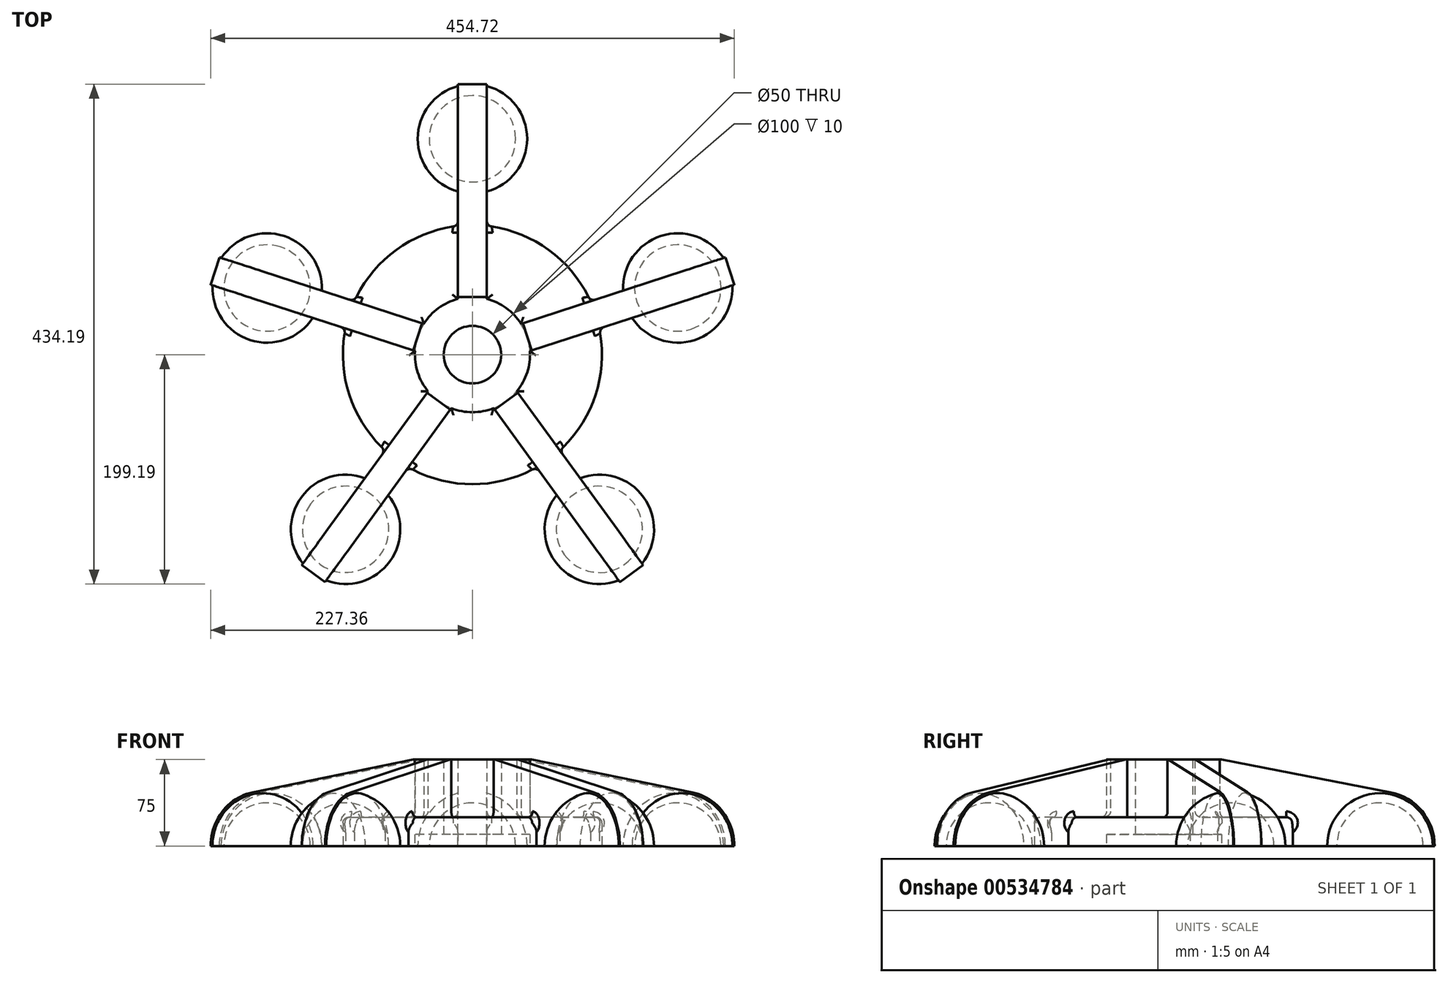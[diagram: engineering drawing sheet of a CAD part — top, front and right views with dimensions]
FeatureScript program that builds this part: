
annotation { "Feature Type Name" : "Feature", "Feature Type Description" : "" }
export const myFeature = defineFeature(function(context is Context, id is Id, definition is map)
    precondition{}
    {
        {
            var Q0;
            Q0=qCreatedBy(makeId("Right.planeOp"),FACE);
            var sketch = newSketch(context, id + "F0", { "sketchPlane" : qUnion([Q0])});
            skCircle(sketch, "E0", {"center": v(187.5, 0) * mm, "radius": 37.5 * mm});
            skCircle(sketch, "E1", {"center": v(187.5, 0) * mm, "radius": 47.5 * mm});
            skLineSegment(sketch, "E2", {"start": v(140, 0) * mm, "end": v(235, 0) * mm});
            skLineSegment(sketch, "E3", {"start": v(187.5, 47.5) * mm, "end": v(187.5, -47.5) * mm});
            skLineSegment(sketch, "E4", {"start": v(0, 0) * mm, "end": v(140, 0) * mm});
            skLineSegment(sketch, "E5", {"start": v(0, 0) * mm, "end": v(0, 75) * mm});
            skLineSegment(sketch, "E6", {"start": v(0, 75) * mm, "end": v(50, 75) * mm});
            skLineSegment(sketch, "E7", {"start": v(50, 75) * mm, "end": v(196.53, 46.63) * mm});
            skSolve(sketch);
        }
        {
            var Q0;
            {var subQ0=sQuery(id+"F0.wireOp",EDGE,"E3");var subQ1=sQuery(id+"F0.wireOp",EDGE,"E0");var subQ2=makeQuery(id+"F0.imprint","INTERSECT",VERTEX,{"disambiguationData":[OD(0.0)],"derivedFrom":[subQ1,subQ0]});Q0=makeQuery(id+"F0.imprint","IMPRINT",FACE,{"disambiguationData":[TD([[makeQuery(id+"F0.imprint","IMPRINT",EDGE,{"disambiguationData":[TD([[subQ2,1.0]])],"derivedFrom":subQ1}),-1.0]])]});}
            var Q1;
            Q1=sQuery(id+"F0.wireOp",EDGE,"E3");
            revolve(context, id + "F1", {"entities" : qUnion([Q0]), "axis" : qUnion([Q1]), "revolveType" : RevolveType.FULL});
        }
        {
            var Q0;
            Q0=qCreatedBy(makeId("Right.planeOp"),FACE);
            var sketch = newSketch(context, id + "F2", { "sketchPlane" : qUnion([Q0])});
            skCircle(sketch, "E8", {"center": v(187.5, 0) * mm, "radius": 37.5 * mm});
            skCircle(sketch, "E9", {"center": v(187.5, 0) * mm, "radius": 47.5 * mm});
            skLineSegment(sketch, "E10", {"start": v(140, 0) * mm, "end": v(235, 0) * mm});
            skLineSegment(sketch, "E11", {"start": v(187.5, 47.5) * mm, "end": v(187.5, -47.5) * mm});
            skLineSegment(sketch, "E12", {"start": v(0, 0) * mm, "end": v(140, 0) * mm});
            skLineSegment(sketch, "E13", {"start": v(0, 0) * mm, "end": v(0, 75) * mm});
            skLineSegment(sketch, "E14", {"start": v(0, 75) * mm, "end": v(50, 75) * mm});
            skLineSegment(sketch, "E15", {"start": v(50, 75) * mm, "end": v(196.53, 46.63) * mm});
            skSolve(sketch);
        }
        {
            var Q0;
            {var subQ0=sQuery(id+"F2.wireOp",EDGE,"E12");Q0=makeQuery(id+"F2.imprint","IMPRINT",FACE,{"disambiguationData":[TD([[makeQuery(id+"F2.imprint","IMPRINT",EDGE,{"derivedFrom":subQ0}),1.0]])]});}
            var Q1;
            {var subQ3=sQuery(id+"F2.wireOp",EDGE,"E8");var subQ6=sQuery(id+"F2.wireOp",EDGE,"E11");var subQ8=makeQuery(id+"F2.imprint","INTERSECT",VERTEX,{"disambiguationData":[OD(0.0)],"derivedFrom":[subQ3,subQ6]});Q1=makeQuery(id+"F2.imprint","IMPRINT",FACE,{"disambiguationData":[TD([[makeQuery(id+"F2.imprint","IMPRINT",EDGE,{"disambiguationData":[TD([[subQ8,1.0]])],"derivedFrom":subQ3}),-1.0]])]});}
            var Q2;
            {var subQ0=sQuery(id+"F2.wireOp",EDGE,"E11");var subQ1=sQuery(id+"F2.wireOp",EDGE,"E8");var subQ2=makeQuery(id+"F2.imprint","INTERSECT",VERTEX,{"disambiguationData":[OD(0.0)],"derivedFrom":[subQ1,subQ0]});Q2=makeQuery(id+"F2.imprint","IMPRINT",FACE,{"disambiguationData":[TD([[makeQuery(id+"F2.imprint","IMPRINT",EDGE,{"disambiguationData":[TD([[subQ2,-1.0]])],"derivedFrom":subQ1}),-1.0]])]});}
            extrude(context, id + "F3", {"entities" : qUnion([Q0, Q1, Q2]), "operationType" : NewBodyOperationType.ADD, "endBound" : BoundingType.SYMMETRIC, "depth" : 25 * mm, "offsetDistance" : 25 * mm});
        }
        {
            var Q0;
            Q0=qCreatedBy(makeId("Top.planeOp"),FACE);
            var sketch = newSketch(context, id + "F4", { "sketchPlane" : qUnion([Q0])});
            skCircle(sketch, "E16", {"center": v(0, 0) * mm, "radius": 25 * mm});
            skCircle(sketch, "E17", {"center": v(0, 0) * mm, "radius": 50 * mm});
            skSolve(sketch);
        }
        {
            var Q0;
            Q0=makeQuery(id+"F4.imprint","IMPRINT",FACE,{"disambiguationData":[TD([[makeQuery(id+"F4.imprint","IMPRINT",EDGE,{"derivedFrom":sQuery(id+"F4.wireOp",EDGE,"E16")}),1.0]])]});
            extrude(context, id + "F5", {"entities" : qUnion([Q0]), "operationType" : NewBodyOperationType.REMOVE, "endBound" : BoundingType.THROUGH_ALL, "depth" : 25 * mm, "offsetDistance" : 25 * mm});
        }
        {
            var Q0;
            Q0=qCreatedBy(makeId("Top.planeOp"),FACE);
            var sketch = newSketch(context, id + "F6", { "sketchPlane" : qUnion([Q0])});
            skCircle(sketch, "E18", {"center": v(0, 0) * mm, "radius": 50 * mm});
            skCircle(sketch, "E19", {"center": v(0, 0) * mm, "radius": 25 * mm});
            skSolve(sketch);
        }
        {
            var Q0;
            Q0 = qSketchRegion(id + "F6", true);
            var Q1;
            Q1=makeQuery(id+"F3.opExtrude","SWEPT_FACE",FACE,{"disambiguationData":[OSD([sQuery(id+"F2.wireOp",EDGE,"E14")])]});
            extrude(context, id + "F7", {"entities" : qUnion([Q0]), "operationType" : NewBodyOperationType.ADD, "endBound" : BoundingType.UP_TO_SURFACE, "depth" : 25 * mm, "endBoundEntityFace" : qUnion([Q1]), "offsetDistance" : 25 * mm});
        }
        {
            var Q0;
            Q0=makeQuery(id+"F1.opRevolve","SWEPT_BODY",BODY,{"disambiguationData":[OSD([sQuery(id+"F0.wireOp",EDGE,"E0"),sQuery(id+"F0.wireOp",EDGE,"E1"),sQuery(id+"F0.wireOp",EDGE,"E2"),sQuery(id+"F0.wireOp",EDGE,"E3")])]});
            var Q1;
            Q1=makeQuery(id+"F5.boolean.opBoolean","COPY",FACE,{"derivedFrom":makeQuery(id+"F5.opExtrude","SWEPT_FACE",FACE,{"disambiguationData":[OSD([sQuery(id+"F4.wireOp",EDGE,"E16")])]})});
            circularPattern(context, id + "F8", {"operationType" : NewBodyOperationType.ADD, "entities" : qUnion([Q0]), "axis" : qUnion([Q1]), "angle" : 360 * degree, "instanceCount" : 5, "equalSpace" : true});
        }
        {
            var Q0;
            Q0=qCreatedBy(makeId("Top.planeOp"),FACE);
            var sketch = newSketch(context, id + "F9", { "sketchPlane" : qUnion([Q0])});
            skCircle(sketch, "E20", {"center": v(0, 0) * mm, "radius": 112.5 * mm});
            skCircle(sketch, "E21", {"center": v(0, 0) * mm, "radius": 25 * mm});
            skSolve(sketch);
        }
        {
            var Q0;
            Q0=makeQuery(id+"F9.imprint","IMPRINT",FACE,{"disambiguationData":[TD([[makeQuery(id+"F9.imprint","IMPRINT",EDGE,{"derivedFrom":sQuery(id+"F9.wireOp",EDGE,"E20")}),1.0]])]});
            extrude(context, id + "F10", {"entities" : qUnion([Q0]), "operationType" : NewBodyOperationType.ADD, "depth" : 25 * mm, "offsetDistance" : 25 * mm});
        }
        {
            var Q0;
            {var subQ0=sQuery(id+"F2.wireOp",EDGE,"E15");var subQ1=sQuery(id+"F2.wireOp",EDGE,"E14");var subQ2=sQuery(id+"F2.wireOp",EDGE,"E13");var subQ3=sQuery(id+"F2.wireOp",EDGE,"E12");var subQ4=sQuery(id+"F2.wireOp",EDGE,"E10");var subQ5=sQuery(id+"F2.wireOp",EDGE,"E9");var subQ6=sQuery(id+"F2.wireOp",EDGE,"E8");var subQ7=sQuery(id+"F9.wireOp",EDGE,"E20");Q0=makeQuery(id+"F10.boolean.opBoolean","SPLIT",FACE,{"disambiguationData":[TD([makeQuery(id+"F3.opExtrude","CAP_FACE",FACE,{"disambiguationData":[OSD([subQ6,subQ5,subQ4,subQ3,subQ2,subQ1,subQ0])],"isStart":true})])],"derivedFrom":makeQuery(id+"F10.opExtrude","CAP_FACE",FACE,{"disambiguationData":[OSD([subQ7,sQuery(id+"F9.wireOp",EDGE,"MwNo4NWU-MyD3-ABLd-Lk5J-k6dSSuvND8tt")])],"isStart":false})});}
            var Q1;
            {var subQ0=sQuery(id+"F9.wireOp",EDGE,"E20");var subQ1=sQuery(id+"F2.wireOp",EDGE,"E15");var subQ2=sQuery(id+"F2.wireOp",EDGE,"E14");var subQ3=sQuery(id+"F2.wireOp",EDGE,"E13");var subQ4=sQuery(id+"F2.wireOp",EDGE,"E12");var subQ5=sQuery(id+"F2.wireOp",EDGE,"E10");var subQ6=sQuery(id+"F2.wireOp",EDGE,"E9");var subQ7=sQuery(id+"F2.wireOp",EDGE,"E8");Q1=makeQuery(id+"F10.boolean.opBoolean","SPLIT",FACE,{"disambiguationData":[TD([makeQuery(id+"F8.opPattern","COPY",FACE,{"derivedFrom":makeQuery(id+"F3.opExtrude","CAP_FACE",FACE,{"disambiguationData":[OSD([subQ7,subQ6,subQ5,subQ4,subQ3,subQ2,subQ1])],"isStart":true}),"instanceName":"1"})])],"derivedFrom":makeQuery(id+"F10.opExtrude","CAP_FACE",FACE,{"disambiguationData":[OSD([subQ0,sQuery(id+"F9.wireOp",EDGE,"MwNo4NWU-MyD3-ABLd-Lk5J-k6dSSuvND8tt")])],"isStart":false})});}
            var Q2;
            {var subQ0=sQuery(id+"F2.wireOp",EDGE,"E15");var subQ1=sQuery(id+"F2.wireOp",EDGE,"E14");var subQ2=sQuery(id+"F2.wireOp",EDGE,"E13");var subQ3=sQuery(id+"F2.wireOp",EDGE,"E12");var subQ4=sQuery(id+"F2.wireOp",EDGE,"E10");var subQ5=sQuery(id+"F2.wireOp",EDGE,"E9");var subQ6=sQuery(id+"F2.wireOp",EDGE,"E8");var subQ7=sQuery(id+"F9.wireOp",EDGE,"E20");Q2=makeQuery(id+"F10.boolean.opBoolean","SPLIT",FACE,{"disambiguationData":[TD([makeQuery(id+"F8.opPattern","COPY",FACE,{"derivedFrom":makeQuery(id+"F3.opExtrude","CAP_FACE",FACE,{"disambiguationData":[OSD([subQ6,subQ5,subQ4,subQ3,subQ2,subQ1,subQ0])],"isStart":true}),"instanceName":"2"})])],"derivedFrom":makeQuery(id+"F10.opExtrude","CAP_FACE",FACE,{"disambiguationData":[OSD([subQ7,sQuery(id+"F9.wireOp",EDGE,"MwNo4NWU-MyD3-ABLd-Lk5J-k6dSSuvND8tt")])],"isStart":false})});}
            var Q3;
            {var subQ0=sQuery(id+"F9.wireOp",EDGE,"E20");var subQ1=sQuery(id+"F2.wireOp",EDGE,"E15");var subQ2=sQuery(id+"F2.wireOp",EDGE,"E14");var subQ3=sQuery(id+"F2.wireOp",EDGE,"E13");var subQ4=sQuery(id+"F2.wireOp",EDGE,"E12");var subQ5=sQuery(id+"F2.wireOp",EDGE,"E10");var subQ6=sQuery(id+"F2.wireOp",EDGE,"E9");var subQ7=sQuery(id+"F2.wireOp",EDGE,"E8");Q3=makeQuery(id+"F10.boolean.opBoolean","SPLIT",FACE,{"disambiguationData":[TD([makeQuery(id+"F8.opPattern","COPY",FACE,{"derivedFrom":makeQuery(id+"F3.opExtrude","CAP_FACE",FACE,{"disambiguationData":[OSD([subQ7,subQ6,subQ5,subQ4,subQ3,subQ2,subQ1])],"isStart":true}),"instanceName":"3"})])],"derivedFrom":makeQuery(id+"F10.opExtrude","CAP_FACE",FACE,{"disambiguationData":[OSD([subQ0,sQuery(id+"F9.wireOp",EDGE,"MwNo4NWU-MyD3-ABLd-Lk5J-k6dSSuvND8tt")])],"isStart":false})});}
            var Q4;
            {var subQ0=sQuery(id+"F2.wireOp",EDGE,"E15");var subQ1=sQuery(id+"F2.wireOp",EDGE,"E14");var subQ2=sQuery(id+"F2.wireOp",EDGE,"E13");var subQ3=sQuery(id+"F2.wireOp",EDGE,"E12");var subQ4=sQuery(id+"F2.wireOp",EDGE,"E10");var subQ5=sQuery(id+"F2.wireOp",EDGE,"E9");var subQ6=sQuery(id+"F2.wireOp",EDGE,"E8");var subQ7=sQuery(id+"F9.wireOp",EDGE,"E20");Q4=makeQuery(id+"F10.boolean.opBoolean","SPLIT",FACE,{"disambiguationData":[TD([makeQuery(id+"F3.opExtrude","CAP_FACE",FACE,{"disambiguationData":[OSD([subQ6,subQ5,subQ4,subQ3,subQ2,subQ1,subQ0])],"isStart":false})])],"derivedFrom":makeQuery(id+"F10.opExtrude","CAP_FACE",FACE,{"disambiguationData":[OSD([subQ7,sQuery(id+"F9.wireOp",EDGE,"MwNo4NWU-MyD3-ABLd-Lk5J-k6dSSuvND8tt")])],"isStart":false})});}
            var Q5;
            Q5=makeQuery(id+"F10.boolean.opBoolean","INTERSECT",EDGE,{"derivedFrom":[makeQuery(id+"F8.opPattern","COPY",FACE,{"derivedFrom":makeQuery(id+"F3.opExtrude","CAP_FACE",FACE,{"disambiguationData":[OSD([sQuery(id+"F2.wireOp",EDGE,"E8"),sQuery(id+"F2.wireOp",EDGE,"E9"),sQuery(id+"F2.wireOp",EDGE,"E10"),sQuery(id+"F2.wireOp",EDGE,"E12"),sQuery(id+"F2.wireOp",EDGE,"E13"),sQuery(id+"F2.wireOp",EDGE,"E14"),sQuery(id+"F2.wireOp",EDGE,"E15")])],"isStart":false}),"instanceName":"2"}),makeQuery(id+"F10.opExtrude","CAP_FACE",FACE,{"disambiguationData":[OSD([sQuery(id+"F9.wireOp",EDGE,"E20"),sQuery(id+"F9.wireOp",EDGE,"MwNo4NWU-MyD3-ABLd-Lk5J-k6dSSuvND8tt")])],"isStart":false})]});
            fillet(context, id + "F11", {"entities" : qUnion([Q0, Q1, Q2, Q3, Q4, Q5]), "radius" : 5 * mm, "tangentPropagation" : true, "allowEdgeOverflow" : false});
        }
        {
            var Q0;
            Q0=qCreatedBy(makeId("Top.planeOp"),FACE);
            var sketch = newSketch(context, id + "F12", { "sketchPlane" : qUnion([Q0])});
            skCircle(sketch, "E22", {"center": v(0, 0) * mm, "radius": 50 * mm});
            skSolve(sketch);
        }
        {
            var Q0;
            Q0 = qSketchRegion(id + "F12", true);
            extrude(context, id + "F13", {"entities" : qUnion([Q0]), "operationType" : NewBodyOperationType.REMOVE, "depth" : 10 * mm, "offsetDistance" : 25 * mm});
        }
    });
